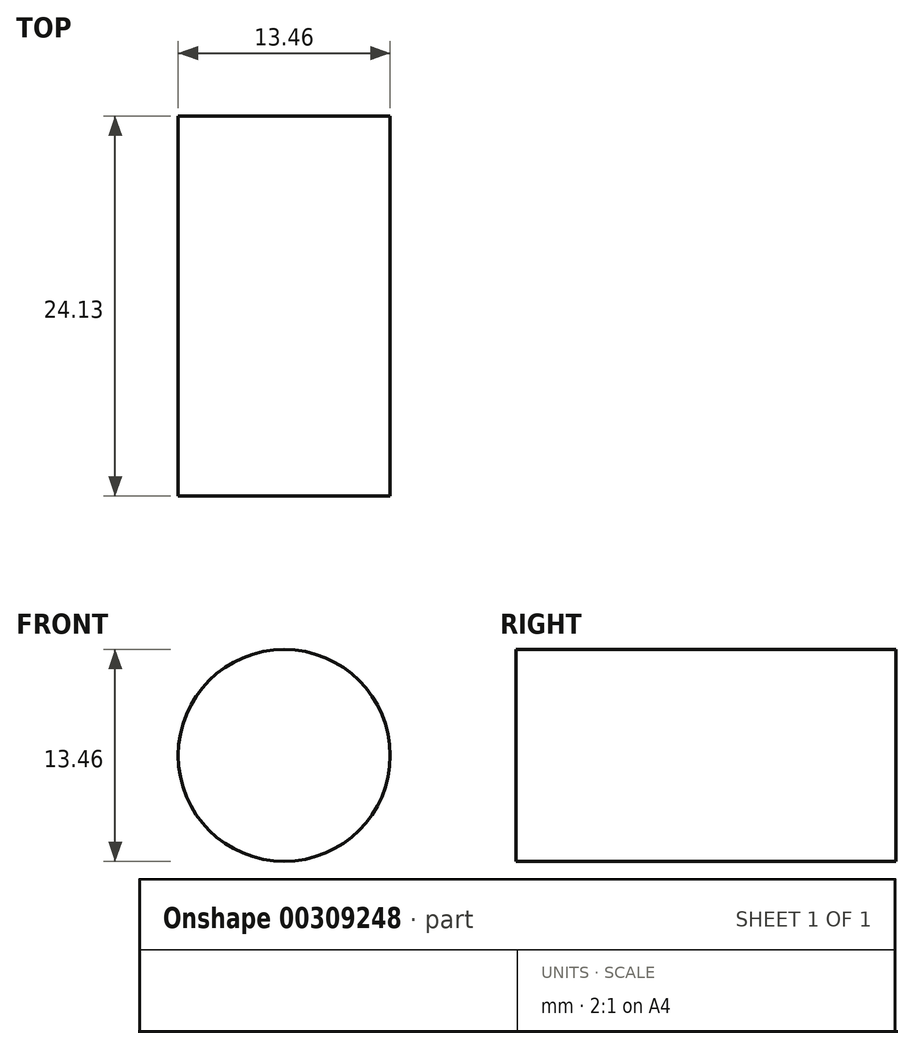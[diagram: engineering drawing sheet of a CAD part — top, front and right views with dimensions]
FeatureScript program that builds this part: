
annotation { "Feature Type Name" : "Feature", "Feature Type Description" : "" }
export const myFeature = defineFeature(function(context is Context, id is Id, definition is map)
    precondition{}
    {
        {
            var Q0;
            Q0=qCreatedBy(makeId("Front.planeOp"),FACE);
            var sketch = newSketch(context, id + "F0", { "sketchPlane" : qUnion([Q0])});
            skCircle(sketch, "E0", {"center": v(0, 0) * mm, "radius": 6.73 * mm});
            skSolve(sketch);
        }
        {
            var Q0;
            Q0=sQuery(id+"F0.wireOp",EDGE,"E0");
            extrude(context, id + "F1", {"bodyType" : ToolBodyType.SURFACE, "surfaceEntities" : qUnion([Q0]), "depth" : 24.13 * mm});
        }
    });
